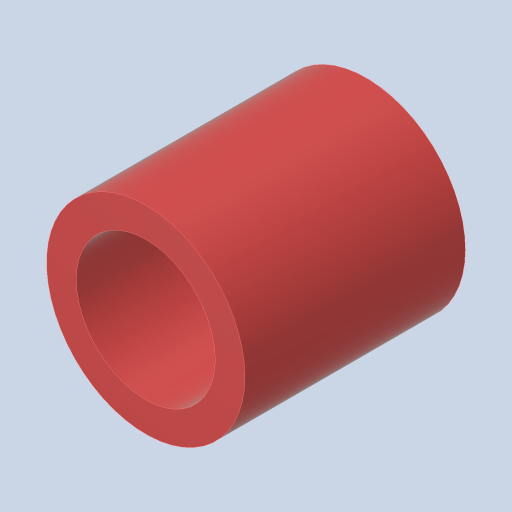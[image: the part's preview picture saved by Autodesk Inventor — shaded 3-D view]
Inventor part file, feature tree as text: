
AUTODESK INVENTOR PART (.ipt)
format: ipt  version: 2023.4 (Build 274418000, 418)  size: 123,904 bytes
history: native  units: in
note: dims shown in document units (in); Inventor stores cm internally (conversion verified against a paired STEP export)
features: extrude x1, sketch x1
ambient origin geometry x8: Origin, YZ Plane, XZ Plane, XY Plane, X Axis, Y Axis, Z Axis, Center Point
bodies: Solid1 (feature_tree)
feature tree (2):
  extrude  "Extrusion1"  Depth=0.928in
  sketch  "Sketch1"  dims[d0=0.585in d1=0.125in d2=0.928in d3=0.0in]
